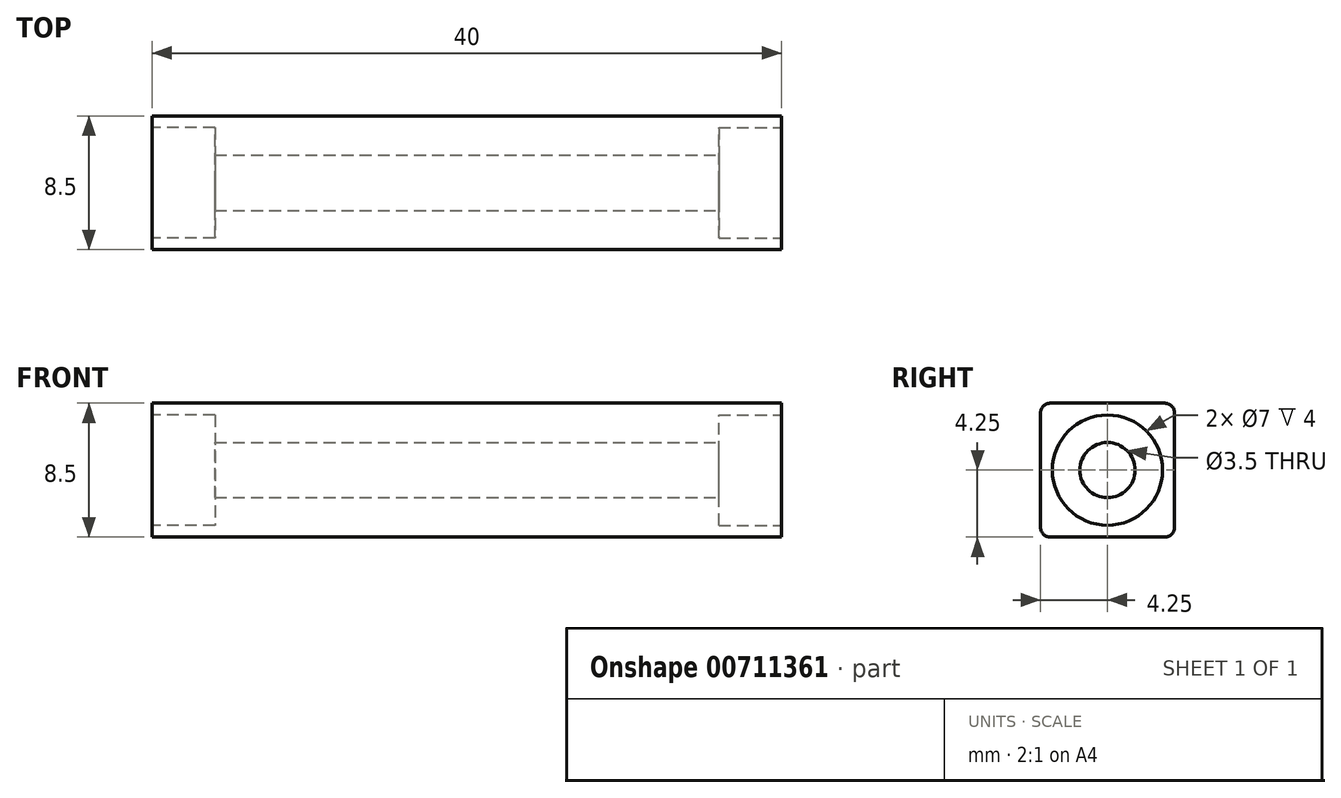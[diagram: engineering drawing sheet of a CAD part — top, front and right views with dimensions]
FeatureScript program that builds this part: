
annotation { "Feature Type Name" : "Feature", "Feature Type Description" : "" }
export const myFeature = defineFeature(function(context is Context, id is Id, definition is map)
    precondition{}
    {
        {
            var Q0;
            Q0=qCreatedBy(makeId("Top.planeOp"),FACE);
            var sketch = newSketch(context, id + "F0", { "sketchPlane" : qUnion([Q0])});
            skLineSegment(sketch, "E0.bottom", {"start": v(20, -4.25) * mm, "end": v(-20, -4.25) * mm});
            skLineSegment(sketch, "E0.top", {"start": v(20, 4.25) * mm, "end": v(-20, 4.25) * mm});
            skLineSegment(sketch, "E0.left", {"start": v(20, -4.25) * mm, "end": v(20, 4.25) * mm});
            skLineSegment(sketch, "E0.right", {"start": v(-20, -4.25) * mm, "end": v(-20, 4.25) * mm});
            skPoint(sketch, "E0.middle", {"position": v(0, 0) * mm});
            skSolve(sketch);
        }
        {
            var Q0;
            Q0=makeQuery(id+"F0.imprint","IMPRINT",FACE,{"disambiguationData":[TD([[makeQuery(id+"F0.imprint","IMPRINT",EDGE,{"derivedFrom":sQuery(id+"F0.wireOp",EDGE,"E0.bottom")}),-1.0]])]});
            extrude(context, id + "F1", {"entities" : qUnion([Q0]), "depth" : 8.5 * mm, "offsetDistance" : 25 * mm});
        }
        {
            var Q0;
            Q0=makeQuery(id+"F1.opExtrude","SWEPT_FACE",FACE,{"disambiguationData":[OSD([sQuery(id+"F0.wireOp",EDGE,"E0.left")])]});
            var sketch = newSketch(context, id + "F2", { "sketchPlane" : qUnion([Q0])});
            skLineSegment(sketch, "E1", {"start": v(4.25, 8.5) * mm, "end": v(-4.25, 0) * mm, "construction": true});
            skLineSegment(sketch, "E2", {"start": v(-4.25, 8.5) * mm, "end": v(4.25, 0) * mm, "construction": true});
            skPoint(sketch, "E3", {"position": v(0, 4.25) * mm});
            skCircle(sketch, "E4", {"center": v(0, 4.25) * mm, "radius": 3.5 * mm});
            skCircle(sketch, "E5", {"center": v(0, 4.25) * mm, "radius": 1.75 * mm});
            skSolve(sketch);
        }
        {
            var Q0;
            Q0=makeQuery(id+"F2.imprint","IMPRINT",FACE,{"disambiguationData":[TD([[makeQuery(id+"F2.imprint","IMPRINT",EDGE,{"derivedFrom":sQuery(id+"F2.wireOp",EDGE,"E5")}),1.0]])]});
            extrude(context, id + "F3", {"entities" : qUnion([Q0]), "operationType" : NewBodyOperationType.REMOVE, "oppositeDirection" : true, "depth" : 40 * mm, "offsetDistance" : 25 * mm});
        }
        {
            var Q0;
            Q0=makeQuery(id+"F2.imprint","IMPRINT",FACE,{"disambiguationData":[TD([[makeQuery(id+"F2.imprint","IMPRINT",EDGE,{"derivedFrom":sQuery(id+"F2.wireOp",EDGE,"E4")}),1.0]])]});
            extrude(context, id + "F4", {"entities" : qUnion([Q0]), "operationType" : NewBodyOperationType.REMOVE, "oppositeDirection" : true, "depth" : 4 * mm, "offsetDistance" : 25 * mm});
        }
        {
            var Q0;
            Q0=makeQuery(id+"F1.opExtrude","SWEPT_FACE",FACE,{"disambiguationData":[OSD([sQuery(id+"F0.wireOp",EDGE,"E0.right")])]});
            var sketch = newSketch(context, id + "F5", { "sketchPlane" : qUnion([Q0])});
            skCircle(sketch, "E6", {"center": v(0, 4.25) * mm, "radius": 3.5 * mm});
            skSolve(sketch);
        }
        {
            var Q0;
            Q0=makeQuery(id+"F5.imprint","IMPRINT",FACE,{"disambiguationData":[TD([[makeQuery(id+"F5.imprint","IMPRINT",EDGE,{"derivedFrom":sQuery(id+"F5.wireOp",EDGE,"E6")}),1.0]])]});
            extrude(context, id + "F6", {"entities" : qUnion([Q0]), "operationType" : NewBodyOperationType.REMOVE, "oppositeDirection" : true, "depth" : 4 * mm, "offsetDistance" : 25 * mm});
        }
        {
            var Q0;
            Q0=makeQuery(id+"F1.opExtrude","CAP_EDGE",EDGE,{"disambiguationData":[OSD([sQuery(id+"F0.wireOp",EDGE,"E0.top")])],"isStart":false});
            var Q1;
            Q1=makeQuery(id+"F1.opExtrude","CAP_EDGE",EDGE,{"disambiguationData":[OSD([sQuery(id+"F0.wireOp",EDGE,"E0.top")])],"isStart":true});
            var Q2;
            Q2=makeQuery(id+"F1.opExtrude","CAP_EDGE",EDGE,{"disambiguationData":[OSD([sQuery(id+"F0.wireOp",EDGE,"E0.bottom")])],"isStart":false});
            var Q3;
            Q3=makeQuery(id+"F1.opExtrude","CAP_EDGE",EDGE,{"disambiguationData":[OSD([sQuery(id+"F0.wireOp",EDGE,"E0.bottom")])],"isStart":true});
            fillet(context, id + "F7", {"entities" : qUnion([Q0, Q1, Q2, Q3]), "radius" : 0.6 * mm, "tangentPropagation" : true, "allowEdgeOverflow" : false});
        }
    });
